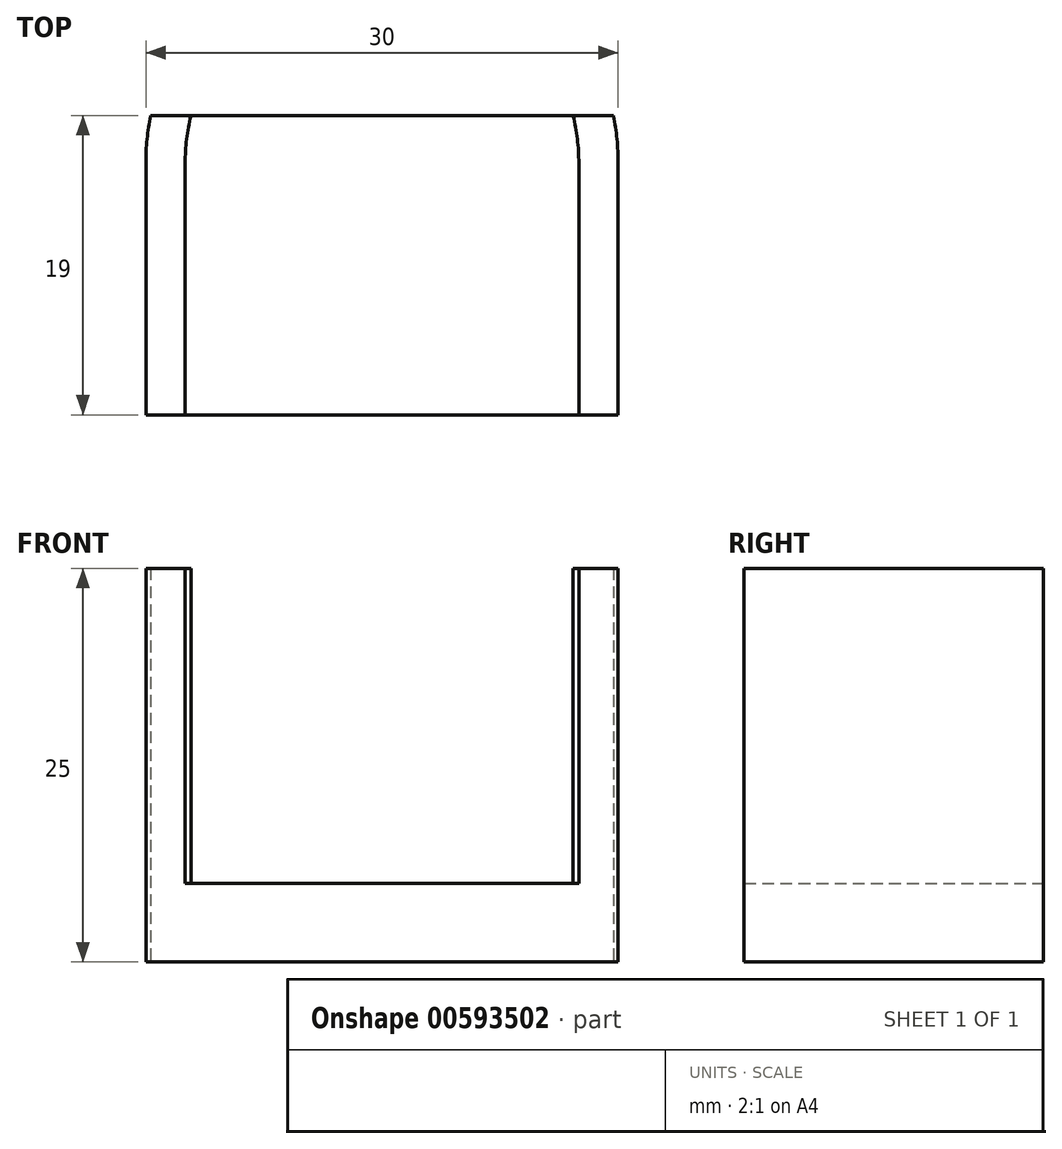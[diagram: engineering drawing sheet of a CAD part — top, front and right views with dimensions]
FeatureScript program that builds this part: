
annotation { "Feature Type Name" : "Feature", "Feature Type Description" : "" }
export const myFeature = defineFeature(function(context is Context, id is Id, definition is map)
    precondition{}
    {
        {
            var Q0;
            Q0=qCreatedBy(makeId("Top.planeOp"),FACE);
            var sketch = newSketch(context, id + "F0", { "sketchPlane" : qUnion([Q0])});
            skArc(sketch, "E0", {"start": v(-12.13, 3) * mm, "mid": v(0, -12.5) * mm, "end": v(12.13, 3) * mm});
            skArc(sketch, "E1", {"start": v(-14.7, 3) * mm, "mid": v(0, -15) * mm, "end": v(14.7, 3) * mm});
            skLineSegment(sketch, "E2", {"start": v(-15, 0) * mm, "end": v(-15, -16) * mm});
            skLineSegment(sketch, "E3", {"start": v(-15, -16) * mm, "end": v(15, -16) * mm});
            skLineSegment(sketch, "E4", {"start": v(15, -16) * mm, "end": v(15, 0) * mm});
            skLineSegment(sketch, "E5", {"start": v(0, 0) * mm, "end": v(0, 3) * mm});
            skLineSegment(sketch, "E6", {"start": v(0, 3) * mm, "end": v(-14.7, 3) * mm});
            skLineSegment(sketch, "E7", {"start": v(0, 3) * mm, "end": v(14.7, 3) * mm});
            skSolve(sketch);
        }
        {
            var Q0;
            {var subQ0=sQuery(id+"F0.wireOp",EDGE,"E0");Q0=makeQuery(id+"F0.imprint","IMPRINT",FACE,{"disambiguationData":[TD([[makeQuery(id+"F0.imprint","IMPRINT",EDGE,{"derivedFrom":subQ0}),1.0]])]});}
            var Q1;
            {var subQ7=sQuery(id+"F0.wireOp",EDGE,"E0");Q1=makeQuery(id+"F0.imprint","IMPRINT",FACE,{"disambiguationData":[TD([[makeQuery(id+"F0.imprint","IMPRINT",EDGE,{"derivedFrom":subQ7}),-1.0]])]});}
            var Q2;
            {var subQ0=sQuery(id+"F0.wireOp",EDGE,"E2");Q2=makeQuery(id+"F0.imprint","IMPRINT",FACE,{"disambiguationData":[TD([[makeQuery(id+"F0.imprint","IMPRINT",EDGE,{"derivedFrom":subQ0}),1.0]])]});}
            extrude(context, id + "F1", {"entities" : qUnion([Q0, Q1, Q2]), "depth" : 25 * mm, "offsetDistance" : 25 * mm});
        }
        {
            var Q0;
            Q0=makeQuery(id+"F1.opExtrude","CAP_FACE",FACE,{"disambiguationData":[OSD([sQuery(id+"F0.wireOp",EDGE,"E1"),sQuery(id+"F0.wireOp",EDGE,"E2"),sQuery(id+"F0.wireOp",EDGE,"E3"),sQuery(id+"F0.wireOp",EDGE,"E4"),sQuery(id+"F0.wireOp",EDGE,"E6"),sQuery(id+"F0.wireOp",EDGE,"E7")])],"isStart":false});
            var sketch = newSketch(context, id + "F2", { "sketchPlane" : qUnion([Q0])});
            skCircle(sketch, "E8", {"center": v(0, 0) * mm, "radius": 12.5 * mm});
            skLineSegment(sketch, "E9", {"start": v(-12.5, 0) * mm, "end": v(-12.5, -16) * mm});
            skLineSegment(sketch, "E10", {"start": v(-12.5, -16) * mm, "end": v(12.5, -16) * mm});
            skLineSegment(sketch, "E11", {"start": v(12.5, -16) * mm, "end": v(12.5, 0) * mm});
            skSolve(sketch);
        }
        {
            var Q0;
            {var subQ0=sQuery(id+"F2.wireOp",EDGE,"E9");Q0=makeQuery(id+"F2.imprint","IMPRINT",FACE,{"disambiguationData":[TD([[makeQuery(id+"F2.imprint","IMPRINT",EDGE,{"derivedFrom":subQ0}),1.0]])]});}
            var Q1;
            {var subQ0=sQuery(id+"F2.wireOp",EDGE,"E8");var subQ5=makeQuery(id+"F2.imprint","INTERSECT",VERTEX,{"derivedFrom":[subQ0,sQuery(id+"F2.wireOp",EDGE,"E9")]});Q1=makeQuery(id+"F2.imprint","IMPRINT",FACE,{"disambiguationData":[TD([[makeQuery(id+"F2.imprint","IMPRINT",EDGE,{"disambiguationData":[TD([[subQ5,-1.0]])],"derivedFrom":subQ0}),1.0]])]});}
            extrude(context, id + "F3", {"entities" : qUnion([Q0, Q1]), "operationType" : NewBodyOperationType.REMOVE, "oppositeDirection" : true, "depth" : 20 * mm, "offsetDistance" : 25 * mm});
        }
    });
